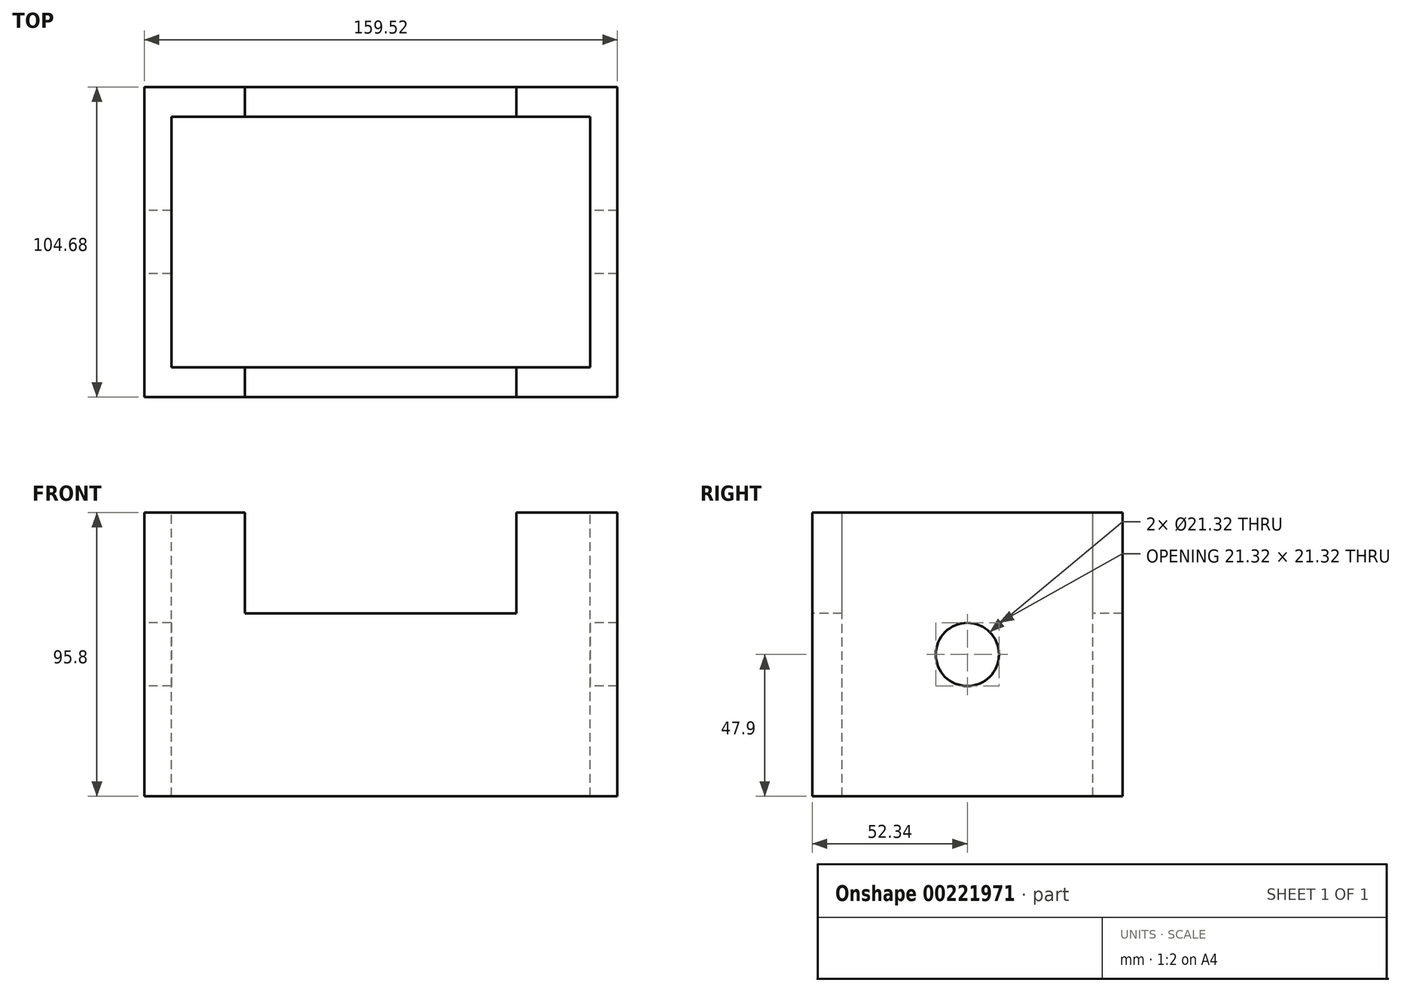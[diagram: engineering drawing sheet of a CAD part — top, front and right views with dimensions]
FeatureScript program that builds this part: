
annotation { "Feature Type Name" : "Feature", "Feature Type Description" : "" }
export const myFeature = defineFeature(function(context is Context, id is Id, definition is map)
    precondition{}
    {
        {
            var Q0;
            Q0=qCreatedBy(makeId("Right.planeOp"),FACE);
            var sketch = newSketch(context, id + "F0", { "sketchPlane" : qUnion([Q0])});
            skLineSegment(sketch, "E0.bottom", {"start": v(52.34, 47.9) * mm, "end": v(-52.34, 47.9) * mm});
            skLineSegment(sketch, "E0.top", {"start": v(52.34, -47.9) * mm, "end": v(-52.34, -47.9) * mm});
            skLineSegment(sketch, "E0.left", {"start": v(52.34, 47.9) * mm, "end": v(52.34, -47.9) * mm});
            skLineSegment(sketch, "E0.right", {"start": v(-52.34, 47.9) * mm, "end": v(-52.34, -47.9) * mm});
            skPoint(sketch, "E0.middle", {"position": v(0, 0) * mm});
            skCircle(sketch, "E1", {"center": v(0, 0) * mm, "radius": 10.66 * mm});
            skSolve(sketch);
        }
        {
            var Q0;
            Q0=makeQuery(id+"F0.imprint","IMPRINT",FACE,{"disambiguationData":[TD([[makeQuery(id+"F0.imprint","IMPRINT",EDGE,{"derivedFrom":sQuery(id+"F0.wireOp",EDGE,"E0.bottom")}),1.0]])]});
            extrude(context, id + "F1", {"entities" : qUnion([Q0]), "endBound" : BoundingType.SYMMETRIC, "depth" : 159.5 * mm});
        }
        {
            var Q0;
            Q0=makeQuery(id+"F1.opExtrude","SWEPT_FACE",FACE,{"disambiguationData":[OSD([sQuery(id+"F0.wireOp",EDGE,"E0.bottom")])]});
            var sketch = newSketch(context, id + "F2", { "sketchPlane" : qUnion([Q0])});
            skLineSegment(sketch, "E2.bottom", {"start": v(70.64, 42.29) * mm, "end": v(-70.64, 42.29) * mm});
            skLineSegment(sketch, "E2.top", {"start": v(70.64, -42.29) * mm, "end": v(-70.64, -42.29) * mm});
            skLineSegment(sketch, "E2.left", {"start": v(70.64, 42.29) * mm, "end": v(70.64, -42.29) * mm});
            skLineSegment(sketch, "E2.right", {"start": v(-70.64, 42.29) * mm, "end": v(-70.64, -42.29) * mm});
            skPoint(sketch, "E2.middle", {"position": v(0, 0) * mm});
            skSolve(sketch);
        }
        {
            var Q0;
            Q0 = qSketchRegion(id + "F2", true);
            extrude(context, id + "F3", {"entities" : qUnion([Q0]), "operationType" : NewBodyOperationType.REMOVE, "oppositeDirection" : true, "depth" : 119.13 * mm});
        }
        {
            var Q0;
            Q0=makeQuery(id+"F1.opExtrude","SWEPT_FACE",FACE,{"disambiguationData":[OSD([sQuery(id+"F0.wireOp",EDGE,"E0.right")])]});
            var sketch = newSketch(context, id + "F4", { "sketchPlane" : qUnion([Q0])});
            skLineSegment(sketch, "E3", {"start": v(0, 47.9) * mm, "end": v(-45.77, 47.9) * mm});
            skLineSegment(sketch, "E4", {"start": v(-45.77, 47.9) * mm, "end": v(-45.77, 13.93) * mm});
            skLineSegment(sketch, "E5", {"start": v(-45.77, 13.93) * mm, "end": v(0, 13.93) * mm});
            skLineSegment(sketch, "E6.MirrorCS", {"start": v(45.77, 13.93) * mm, "end": v(0, 13.93) * mm});
            skLineSegment(sketch, "E7.MirrorCS", {"start": v(45.77, 47.9) * mm, "end": v(45.77, 13.93) * mm});
            skLineSegment(sketch, "E8.MirrorCS", {"start": v(0, 47.9) * mm, "end": v(45.77, 47.9) * mm});
            skSolve(sketch);
        }
        {
            var Q0;
            Q0=makeQuery(id+"F4.imprint","IMPRINT",FACE,{"disambiguationData":[TD([[makeQuery(id+"F4.imprint","IMPRINT",EDGE,{"derivedFrom":sQuery(id+"F4.wireOp",EDGE,"E3")}),1.0]])]});
            extrude(context, id + "F5", {"entities" : qUnion([Q0]), "operationType" : NewBodyOperationType.REMOVE, "oppositeDirection" : true, "depth" : 183.64 * mm});
        }
    });
